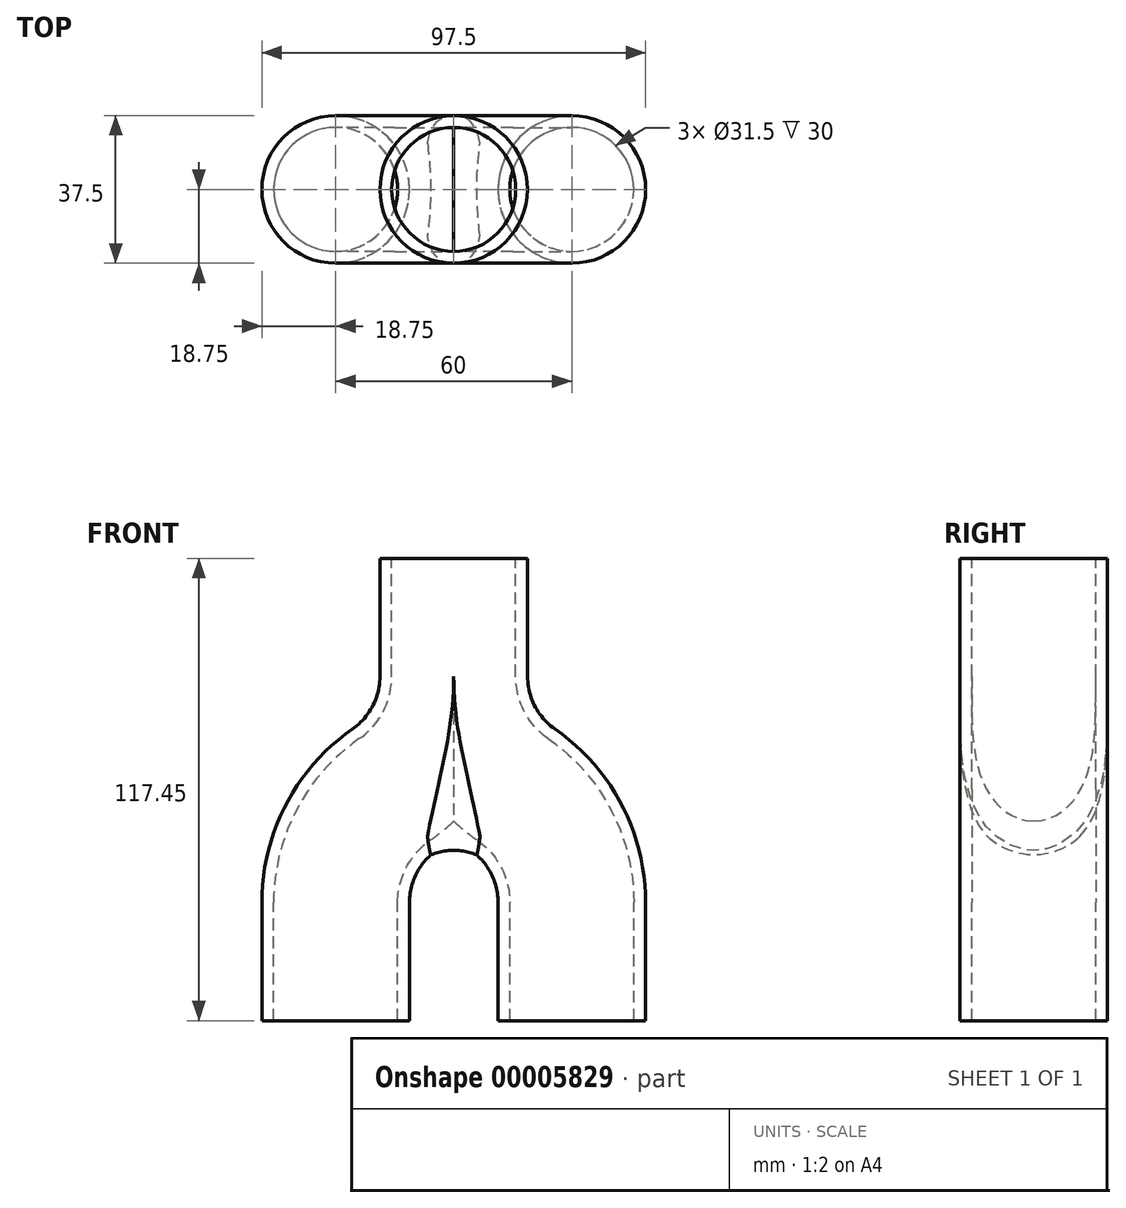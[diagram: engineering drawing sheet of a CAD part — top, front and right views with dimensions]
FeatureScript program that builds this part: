
annotation { "Feature Type Name" : "Feature", "Feature Type Description" : "" }
export const myFeature = defineFeature(function(context is Context, id is Id, definition is map)
    precondition{}
    {
        {
            var Q0;
            Q0=qCreatedBy(makeId("Top.planeOp"),FACE);
            var sketch = newSketch(context, id + "F0", { "sketchPlane" : qUnion([Q0])});
            skCircle(sketch, "E0", {"center": v(-30, 0) * mm, "radius": 18.75 * mm});
            skCircle(sketch, "E1", {"center": v(30, 0) * mm, "radius": 18.75 * mm});
            skLineSegment(sketch, "E2", {"start": v(-30, 0) * mm, "end": v(0, 0) * mm, "construction": true});
            skLineSegment(sketch, "E3", {"start": v(0, 0) * mm, "end": v(30, 0) * mm, "construction": true});
            skCircle(sketch, "E4.0", {"center": v(-30, 0) * mm, "radius": 15.75 * mm});
            skCircle(sketch, "E5.0", {"center": v(30, 0) * mm, "radius": 15.75 * mm});
            skSolve(sketch);
        }
        {
            var Q0;
            Q0=qCreatedBy(makeId("Front.planeOp"),FACE);
            var sketch = newSketch(context, id + "F1", { "sketchPlane" : qUnion([Q0])});
            skPoint(sketch, "E6.0", {"position": v(-30, 0) * mm});
            skLineSegment(sketch, "E7", {"start": v(-30, 0) * mm, "end": v(-30, 30) * mm});
            skLineSegment(sketch, "E8", {"start": v(-15, 58.72) * mm, "end": v(-15, 58.72) * mm});
            skLineSegment(sketch, "E9", {"start": v(0, 87.45) * mm, "end": v(0, 117.45) * mm});
            skPoint(sketch, "E10.visualSharp", {"position": v(0, 69.17) * mm});
            skArc(sketch, "E10.filletArc", {"start": v(-15, 58.72) * mm, "mid": v(-3.98, 71.24) * mm, "end": v(0, 87.45) * mm});
            skPoint(sketch, "E11.visualSharp", {"position": v(-30, 48.28) * mm});
            skArc(sketch, "E11.filletArc", {"start": v(-15, 58.72) * mm, "mid": v(-26.02, 46.2) * mm, "end": v(-30, 30) * mm});
            skLineSegment(sketch, "E12", {"start": v(0, 0) * mm, "end": v(0, 117.45) * mm, "construction": true});
            skLineSegment(sketch, "E13.MirrorCS", {"start": v(15, 58.72) * mm, "end": v(15, 58.72) * mm});
            skLineSegment(sketch, "E14.MirrorCS", {"start": v(30, 0) * mm, "end": v(30, 30) * mm});
            skPoint(sketch, "E15.MirrorP", {"position": v(30, 48.28) * mm});
            skPoint(sketch, "E16.MirrorP", {"position": v(30, 0) * mm});
            skArc(sketch, "E17.MirrorCS", {"start": v(15, 58.72) * mm, "mid": v(26.02, 46.2) * mm, "end": v(30, 30) * mm});
            skArc(sketch, "E18.MirrorCS", {"start": v(15, 58.72) * mm, "mid": v(3.98, 71.24) * mm, "end": v(0, 87.45) * mm});
            skSolve(sketch);
        }
        {
            var Q0;
            Q0=makeQuery(id+"F0.imprint","IMPRINT",FACE,{"disambiguationData":[TD([[makeQuery(id+"F0.imprint","IMPRINT",EDGE,{"derivedFrom":sQuery(id+"F0.wireOp",EDGE,"E0")}),1.0]])]});
            var Q1;
            Q1=sQuery(id+"F1.wireOp",EDGE,"E7");
            var Q2;
            Q2=sQuery(id+"F1.wireOp",EDGE,"E11.filletArc");
            var Q3;
            Q3=sQuery(id+"F1.wireOp",EDGE,"E8");
            var Q4;
            Q4=sQuery(id+"F1.wireOp",EDGE,"E10.filletArc");
            var Q5;
            Q5=sQuery(id+"F1.wireOp",EDGE,"E9");
            sweep(context, id + "F2", {"profiles" : qUnion([Q0]), "path" : qUnion([Q1, Q2, Q3, Q4, Q5])});
        }
        {
            var Q0;
            Q0=qCreatedBy(makeId("Front.planeOp"),FACE);
            var sketch = newSketch(context, id + "F3", { "sketchPlane" : qUnion([Q0])});
            skLineSegment(sketch, "E19.0", {"start": v(-18.75, 117.45) * mm, "end": v(18.75, 117.45) * mm});
            skLineSegment(sketch, "E20.bottom", {"start": v(0, 117.45) * mm, "end": v(31.18, 117.45) * mm});
            skLineSegment(sketch, "E20.top", {"start": v(0, 33.65) * mm, "end": v(31.18, 33.65) * mm});
            skLineSegment(sketch, "E20.left", {"start": v(0, 117.45) * mm, "end": v(0, 33.65) * mm});
            skLineSegment(sketch, "E20.right", {"start": v(31.18, 117.45) * mm, "end": v(31.18, 33.65) * mm});
            skSolve(sketch);
        }
        {
            var Q0;
            Q0=makeQuery(id+"F3.imprint","IMPRINT",FACE,{"disambiguationData":[TD([[makeQuery(id+"F3.imprint","IMPRINT",EDGE,{"derivedFrom":sQuery(id+"F3.wireOp",EDGE,"E20.top")}),1.0]])]});
            extrude(context, id + "F4", {"entities" : qUnion([Q0]), "endBound" : BoundingType.SYMMETRIC, "depth" : 40 * mm, "offsetDistance" : 25 * mm});
        }
        {
            var Q0;
            Q0=makeQuery(id+"F4.opExtrude","SWEPT_BODY",BODY,{"disambiguationData":[OSD([sQuery(id+"F3.wireOp",EDGE,"E20.bottom"),sQuery(id+"F3.wireOp",EDGE,"E20.top"),sQuery(id+"F3.wireOp",EDGE,"E20.left"),sQuery(id+"F3.wireOp",EDGE,"E20.right")])]});
            var Q1;
            Q1=makeQuery(id+"F2.opSweep","SWEPT_BODY",BODY,{"disambiguationData":[OSD([sQuery(id+"F0.wireOp",EDGE,"E0"),sQuery(id+"F0.wireOp",EDGE,"E4.0"),sQuery(id+"F1.wireOp",EDGE,"E9")])]});
            booleanBodies(context, id + "F5", {"operationType" : BooleanOperationType.SUBTRACTION, "tools" : qUnion([Q0]), "targets" : qUnion([Q1])});
        }
        {
            var Q0;
            Q0=makeQuery(id+"F2.opSweep","SWEPT_BODY",BODY,{"disambiguationData":[OSD([sQuery(id+"F0.wireOp",EDGE,"E0"),sQuery(id+"F0.wireOp",EDGE,"E4.0"),sQuery(id+"F1.wireOp",EDGE,"E9")])]});
            var Q1;
            Q1=qCreatedBy(makeId("Right.planeOp"),FACE);
            mirror(context, id + "F6", {"operationType" : NewBodyOperationType.ADD, "entities" : qUnion([Q0]), "mirrorPlane" : qUnion([Q1])});
        }
        {
            var Q0;
            {var subQ0=makeQuery(id+"F5.opBoolean","INTERSECT",EDGE,{"derivedFrom":[makeQuery(id+"F2.opSweep","SWEPT_FACE",FACE,{"disambiguationData":[OSD([sQuery(id+"F0.wireOp",EDGE,"E0"),sQuery(id+"F1.wireOp",EDGE,"E10.filletArc")])]}),makeQuery(id+"F4.opExtrude","SWEPT_FACE",FACE,{"disambiguationData":[OSD([sQuery(id+"F3.wireOp",EDGE,"E20.left")])]})]});Q0=makeQuery(id+"F6.boolean.opBoolean","MERGE",EDGE,{"derivedFrom":[subQ0,makeQuery(id+"F6.opPattern","COPY",EDGE,{"derivedFrom":subQ0,"instanceName":"1"})]});}
            fillet(context, id + "F7", {"entities" : qUnion([Q0]), "radius" : 15 * mm, "tangentPropagation" : true, "allowEdgeOverflow" : false});
        }
    });
